# Revit family: NBS_WallgateLtd_WCPans_CWC-100
name_source: partatom
category: Plumbing Fixtures
revit_build: Autodesk Revit 2014 (Build: 20130709_2115(x64)
units: mm (PartAtom-declared; Revit-internal decimal feet)

## types (1)
- CWC-100
    AssetType = Fixed
    BIMObjectName = NBS_WallgateLtd_WCPans_CWC-100
    ConnectingDimensions = BS EN 33
    Description = Anti-vandal solid surface seatless wall hung pan
    Durability = Compliant to Grade 5
    DurationUnit = year
    Features = Hygienic and easily cleaned, highly vandal-resistant
    Finish = Solid surface
    FixingMaterial = NBS_Concept
    Form = Back to wall, washdown
    IfcExportAs = IfcSanitaryTerminalType
    IfcExportType = TOILETPAN
    IntegralAccessoryOptions = CWC-FRAME-01 Wall Hung WC pan frame, CISTFV Electronic cisterns, FVA Non-Potable Direct Flush Valves, DFKIT Potable Direct Flush Valves, WVC Flush Valve Cables, PBA Piezo Touch Buttons, PBA-IR Infra-Red Activation Sensors, WDC Electronic Controllers
    ManufacturerName = Wallgate Ltd
    ManufacturerURL = www.wallgate.com
    ModelNumber = CWC-100
    NBSCertification = www.nationalbimlibrary.com/cert/5em51xwy
    NBSDescription = WC pans
    NBSReference = 45-35-70/384
    Name = WCPans_CWC-100_WallgateLtd
    NominalDepth = 550 mm
    NominalHeight = 375 mm
    NominalLength = 0 mm  [stored 0 ft]
    NominalWidth = 380 mm
    OperationOptions = Infrared sensor, Piezo touch electronic button, Pneumatic button
    PanColourOptions = MA - Thames, MAH - Frost, MAW - White, MC - Bluestone, MCA - Aubergine, MCB - Diamantina, MCC - Black, MCD - Orange, MCE - Pink, MO - Slate, MS - Hyco, MCJ - Light Grey, MCF - NHS Blue
    PanHeight = 375 mm
    PanMaterial = High-grade solid surface material
    PanMounting = WallHung
    ProductInformation = www.wallgate.com/products/wc-and-toilet-range/cwc-100-series-wall-hung-wc-pans
    Size = 550 x 380 x 375 mm
    SpilloverLevel = 0 mm  [stored 0 ft]
    Standard = BS EN997
    ToiletPanType = Washdown
    ToiletType = LooseCoupled
    Uniclass2 = 45-31-93/494
    Version = 1
    WCMaterial = NBS_Concept
    WarrantyDurationParts = 1
    WarrantyDurationUnit = year
    WaterSupplyOutletAndSeatHolesOutlet = Horizontal back outlet
    WaterSupplyOutletAndSeatHolesWaterSupply = Back inlet
    Weight = 48.5 kg

note: [stored X ft] marks values corroborated as IEEE doubles in the binary element streams (Revit-internal decimal feet)

## geometry (parser evidence)
native form markers: Sweep x1
no freeform markers — native parametric forms only
